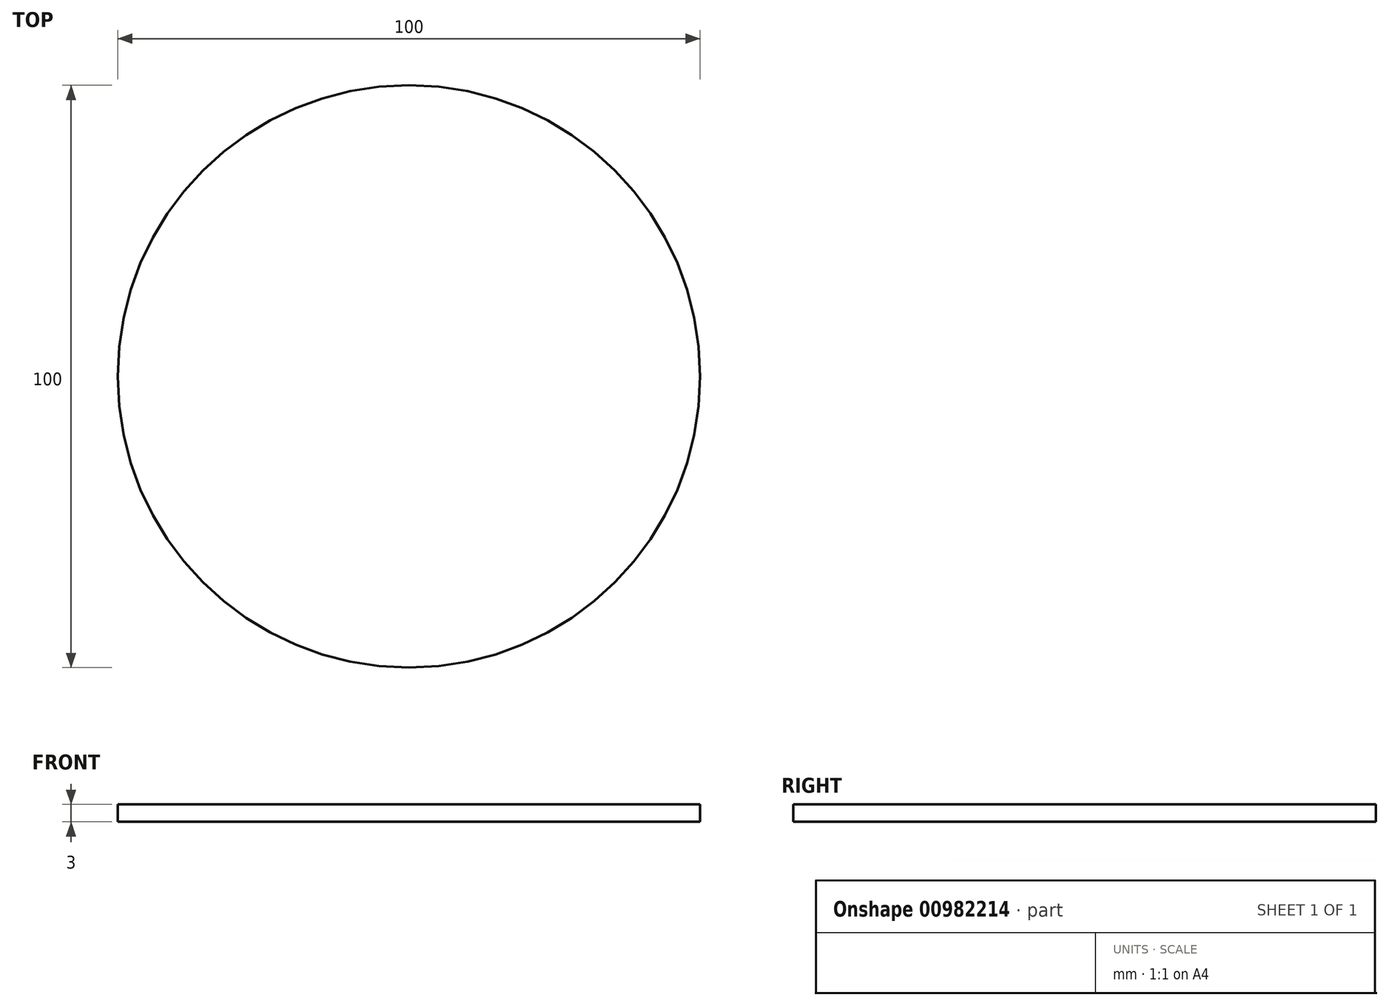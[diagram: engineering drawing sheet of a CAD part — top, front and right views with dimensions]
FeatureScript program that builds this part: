
annotation { "Feature Type Name" : "Feature", "Feature Type Description" : "" }
export const myFeature = defineFeature(function(context is Context, id is Id, definition is map)
    precondition{}
    {
        {
            var Q0;
            Q0=qCreatedBy(makeId("Top.planeOp"),FACE);
            var sketch = newSketch(context, id + "F0", { "sketchPlane" : qUnion([Q0])});
            skCircle(sketch, "E0", {"center": v(0, 0) * mm, "radius": 50 * mm});
            skSolve(sketch);
        }
        {
            var Q0;
            Q0 = qSketchRegion(id + "F0", true);
            extrude(context, id + "F1", {"entities" : qUnion([Q0]), "depth" : 3 * mm, "offsetDistance" : 25 * mm});
        }
    });
